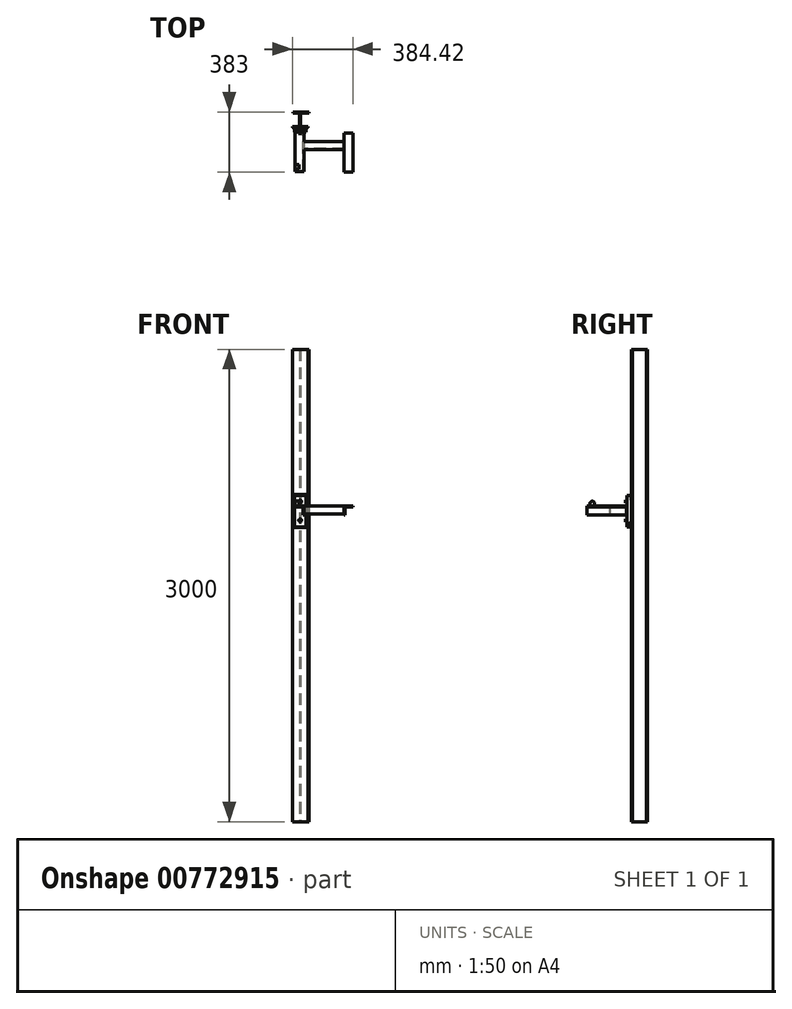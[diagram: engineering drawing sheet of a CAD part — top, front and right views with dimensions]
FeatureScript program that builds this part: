
annotation { "Feature Type Name" : "Feature", "Feature Type Description" : "" }
export const myFeature = defineFeature(function(context is Context, id is Id, definition is map)
    precondition{}
    {
        {
            var Q0;
            Q0=qCreatedBy(makeId("Top.planeOp"),FACE);
            var sketch = newSketch(context, id + "F0", { "sketchPlane" : qUnion([Q0])});
            skLineSegment(sketch, "E0", {"start": v(1.94, 6.65) * mm, "end": v(1.94, 94) * mm});
            skLineSegment(sketch, "E1", {"start": v(1.94, 94) * mm, "end": v(55.47, 94) * mm});
            skLineSegment(sketch, "E2", {"start": v(55.47, 94) * mm, "end": v(55.47, 100) * mm});
            skLineSegment(sketch, "E3", {"start": v(55.47, 100) * mm, "end": v(-44.53, 100) * mm});
            skLineSegment(sketch, "E4", {"start": v(-44.53, 100) * mm, "end": v(-44.53, 94) * mm});
            skLineSegment(sketch, "E5", {"start": v(-44.53, 94) * mm, "end": v(-4.06, 94) * mm});
            skLineSegment(sketch, "E6", {"start": v(-4.06, 94) * mm, "end": v(-4.06, 6.45) * mm});
            skLineSegment(sketch, "E7", {"start": v(-4.06, 6.45) * mm, "end": v(-50, 6.45) * mm});
            skLineSegment(sketch, "E8", {"start": v(-50, 6.45) * mm, "end": v(-50, 0) * mm});
            skLineSegment(sketch, "E9", {"start": v(-50, 0) * mm, "end": v(50, 0) * mm});
            skLineSegment(sketch, "E10", {"start": v(50, 0) * mm, "end": v(50, 6.65) * mm});
            skLineSegment(sketch, "E11", {"start": v(50, 6.65) * mm, "end": v(1.94, 6.65) * mm});
            skSolve(sketch);
        }
        {
            var Q0;
            Q0=makeQuery(id+"F0.imprint","IMPRINT",FACE,{"disambiguationData":[TD([[makeQuery(id+"F0.imprint","IMPRINT",EDGE,{"derivedFrom":sQuery(id+"F0.wireOp",EDGE,"E0")}),1.0]])]});
            extrude(context, id + "F1", {"entities" : qUnion([Q0]), "depth" : 3000 * mm, "offsetDistance" : 25 * mm});
        }
        {
            var Q0;
            Q0=makeQuery(id+"F1.opExtrude","SWEPT_FACE",FACE,{"disambiguationData":[OSD([sQuery(id+"F0.wireOp",EDGE,"E9")])]});
            var sketch = newSketch(context, id + "F2", { "sketchPlane" : qUnion([Q0])});
            skLineSegment(sketch, "E12.bottom", {"start": v(-37.5, 2073.07) * mm, "end": v(37.5, 2073.07) * mm});
            skLineSegment(sketch, "E12.top", {"start": v(-37.5, 1873.07) * mm, "end": v(37.5, 1873.07) * mm});
            skLineSegment(sketch, "E12.left", {"start": v(-37.5, 2073.07) * mm, "end": v(-37.5, 1873.07) * mm});
            skLineSegment(sketch, "E12.right", {"start": v(37.5, 2073.07) * mm, "end": v(37.5, 1873.07) * mm});
            skSolve(sketch);
        }
        {
            var Q0;
            Q0 = qSketchRegion(id + "F2", true);
            extrude(context, id + "F3", {"entities" : qUnion([Q0]), "operationType" : NewBodyOperationType.ADD, "depth" : 20 * mm, "offsetDistance" : 25 * mm});
        }
        {
            var Q0;
            Q0=makeQuery(id+"F3.opExtrude","CAP_FACE",FACE,{"disambiguationData":[OSD([sQuery(id+"F2.wireOp",EDGE,"E12.bottom"),sQuery(id+"F2.wireOp",EDGE,"E12.top"),sQuery(id+"F2.wireOp",EDGE,"E12.left"),sQuery(id+"F2.wireOp",EDGE,"E12.right")])],"isStart":false});
            var sketch = newSketch(context, id + "F4", { "sketchPlane" : qUnion([Q0])});
            skLineSegment(sketch, "E13.bottom", {"start": v(-37.5, 2073.07) * mm, "end": v(37.5, 2073.07) * mm});
            skLineSegment(sketch, "E13.top", {"start": v(-37.5, 1873.07) * mm, "end": v(37.5, 1873.07) * mm});
            skLineSegment(sketch, "E13.left", {"start": v(-37.5, 2073.07) * mm, "end": v(-37.5, 1873.07) * mm});
            skLineSegment(sketch, "E13.right", {"start": v(37.5, 2073.07) * mm, "end": v(37.5, 1873.07) * mm});
            skSolve(sketch);
        }
        {
            var Q0;
            Q0 = qSketchRegion(id + "F4", true);
            extrude(context, id + "F5", {"entities" : qUnion([Q0]), "operationType" : NewBodyOperationType.ADD, "depth" : 9 * mm, "offsetDistance" : 25 * mm});
        }
        {
            var Q0;
            Q0=makeQuery(id+"F5.opExtrude","CAP_FACE",FACE,{"disambiguationData":[OSD([sQuery(id+"F4.wireOp",EDGE,"E13.bottom"),sQuery(id+"F4.wireOp",EDGE,"E13.top"),sQuery(id+"F4.wireOp",EDGE,"E13.left"),sQuery(id+"F4.wireOp",EDGE,"E13.right")])],"isStart":false});
            var sketch = newSketch(context, id + "F6", { "sketchPlane" : qUnion([Q0])});
            skCircle(sketch, "E14", {"center": v(0, 2032.65) * mm, "radius": 9.5 * mm});
            skCircle(sketch, "E15", {"center": v(0, 1914.15) * mm, "radius": 9.29 * mm});
            skPoint(sketch, "E16", {"position": v(0, 2073.07) * mm});
            skSolve(sketch);
        }
        {
            var Q0;
            Q0 = qSketchRegion(id + "F6", true);
            extrude(context, id + "F7", {"entities" : qUnion([Q0]), "operationType" : NewBodyOperationType.ADD, "depth" : 10 * mm, "offsetDistance" : 25 * mm});
        }
        {
            var Q0;
            Q0=makeQuery(id+"F5.opExtrude","CAP_FACE",FACE,{"disambiguationData":[OSD([sQuery(id+"F4.wireOp",EDGE,"E13.bottom"),sQuery(id+"F4.wireOp",EDGE,"E13.top"),sQuery(id+"F4.wireOp",EDGE,"E13.left"),sQuery(id+"F4.wireOp",EDGE,"E13.right")])],"isStart":false});
            var sketch = newSketch(context, id + "F8", { "sketchPlane" : qUnion([Q0])});
            skLineSegment(sketch, "E17.MirrorCS", {"start": v(23.23, 1946.87) * mm, "end": v(16.74, 1946.87) * mm});
            skLineSegment(sketch, "E18.MirrorCS", {"start": v(-31.96, 1998.16) * mm, "end": v(-31.96, 2005.3) * mm});
            skLineSegment(sketch, "E19.MirrorCS", {"start": v(16.74, 1946.87) * mm, "end": v(16.74, 1998.16) * mm});
            skLineSegment(sketch, "E20.MirrorCS", {"start": v(16.74, 1998.16) * mm, "end": v(-31.96, 1998.16) * mm});
            skLineSegment(sketch, "E21.MirrorCS", {"start": v(23.23, 2005.3) * mm, "end": v(23.23, 1946.87) * mm});
            skLineSegment(sketch, "E22.MirrorCS", {"start": v(-31.96, 2005.3) * mm, "end": v(23.23, 2005.3) * mm});
            skSolve(sketch);
        }
        {
            var Q0;
            Q0 = qSketchRegion(id + "F8", true);
            extrude(context, id + "F9", {"entities" : qUnion([Q0]), "operationType" : NewBodyOperationType.ADD, "depth" : 250 * mm, "offsetDistance" : 25 * mm});
        }
        {
            var Q0;
            Q0=makeQuery(id+"F9.opExtrude","SWEPT_FACE",FACE,{"disambiguationData":[OSD([sQuery(id+"F8.wireOp",EDGE,"E21.MirrorCS")])]});
            var sketch = newSketch(context, id + "F10", { "sketchPlane" : qUnion([Q0])});
            skLineSegment(sketch, "E23.MirrorCS", {"start": v(-133, 1955.3) * mm, "end": v(-139, 1955.3) * mm});
            skLineSegment(sketch, "E24.MirrorCS", {"start": v(-89, 1999.3) * mm, "end": v(-89, 2005.3) * mm});
            skLineSegment(sketch, "E25.MirrorCS", {"start": v(-133, 1955.3) * mm, "end": v(-133, 1999.3) * mm});
            skLineSegment(sketch, "E26.MirrorCS", {"start": v(-89, 1999.3) * mm, "end": v(-133, 1999.3) * mm});
            skLineSegment(sketch, "E27.MirrorCS", {"start": v(-139, 2005.3) * mm, "end": v(-139, 1955.3) * mm});
            skLineSegment(sketch, "E28.MirrorCS", {"start": v(-139, 2005.3) * mm, "end": v(-89, 2005.3) * mm});
            skSolve(sketch);
        }
        {
            var Q0;
            Q0 = qSketchRegion(id + "F10", true);
            extrude(context, id + "F11", {"entities" : qUnion([Q0]), "operationType" : NewBodyOperationType.ADD, "depth" : 256 * mm, "offsetDistance" : 25 * mm});
        }
        {
            var Q0;
            Q0=makeQuery(id+"F11.opExtrude","SWEPT_FACE",FACE,{"disambiguationData":[OSD([sQuery(id+"F10.wireOp",EDGE,"E25.MirrorCS")])]});
            var sketch = newSketch(context, id + "F12", { "sketchPlane" : qUnion([Q0])});
            skLineSegment(sketch, "E29.MirrorCS", {"start": v(-279.23, 1946.87) * mm, "end": v(-285.73, 1946.87) * mm});
            skLineSegment(sketch, "E30.MirrorCS", {"start": v(-334.42, 1998.16) * mm, "end": v(-334.42, 2005.3) * mm});
            skLineSegment(sketch, "E31.MirrorCS", {"start": v(-285.73, 1946.87) * mm, "end": v(-285.73, 1998.16) * mm});
            skLineSegment(sketch, "E32.MirrorCS", {"start": v(-285.73, 1998.16) * mm, "end": v(-334.42, 1998.16) * mm});
            skLineSegment(sketch, "E33.MirrorCS", {"start": v(-279.23, 2005.3) * mm, "end": v(-279.23, 1946.87) * mm});
            skLineSegment(sketch, "E34.MirrorCS", {"start": v(-334.42, 2005.3) * mm, "end": v(-279.23, 2005.3) * mm});
            skSolve(sketch);
        }
        {
            var Q0;
            Q0 = qSketchRegion(id + "F12", true);
            extrude(context, id + "F13", {"entities" : qUnion([Q0]), "oppositeDirection" : true, "depth" : 150 * mm, "offsetDistance" : 25 * mm, "hasSecondDirection" : true, "secondDirectionOppositeDirection" : false, "secondDirectionDepth" : 100 * mm});
        }
        {
            var Q0;
            Q0=makeQuery(id+"F1.opExtrude","SWEPT_FACE",FACE,{"disambiguationData":[OSD([sQuery(id+"F0.wireOp",EDGE,"E9")])]});
            var sketch = newSketch(context, id + "F14", { "sketchPlane" : qUnion([Q0])});
            skLineSegment(sketch, "E35.bottom", {"start": v(-43.5, 1904.07) * mm, "end": v(-37.5, 1904.07) * mm});
            skLineSegment(sketch, "E35.top", {"start": v(-43.5, 1873.07) * mm, "end": v(-37.5, 1873.07) * mm});
            skLineSegment(sketch, "E35.left", {"start": v(-43.5, 1904.07) * mm, "end": v(-43.5, 1873.07) * mm});
            skLineSegment(sketch, "E35.right", {"start": v(-37.5, 1904.07) * mm, "end": v(-37.5, 1873.07) * mm});
            skLineSegment(sketch, "E36.bottom", {"start": v(-43.5, 1873.07) * mm, "end": v(43.5, 1873.07) * mm});
            skLineSegment(sketch, "E36.top", {"start": v(-43.5, 1867.07) * mm, "end": v(43.5, 1867.07) * mm});
            skLineSegment(sketch, "E36.left", {"start": v(-43.5, 1873.07) * mm, "end": v(-43.5, 1867.07) * mm});
            skLineSegment(sketch, "E36.right", {"start": v(43.5, 1873.07) * mm, "end": v(43.5, 1867.07) * mm});
            skLineSegment(sketch, "E37.bottom", {"start": v(37.5, 1904.07) * mm, "end": v(43.5, 1904.07) * mm});
            skLineSegment(sketch, "E37.top", {"start": v(37.5, 1873.07) * mm, "end": v(43.5, 1873.07) * mm});
            skLineSegment(sketch, "E37.left", {"start": v(37.5, 1904.07) * mm, "end": v(37.5, 1873.07) * mm});
            skLineSegment(sketch, "E37.right", {"start": v(43.5, 1904.07) * mm, "end": v(43.5, 1873.07) * mm});
            skLineSegment(sketch, "E38.bottom", {"start": v(-37.5, 2042.07) * mm, "end": v(-43.5, 2042.07) * mm});
            skLineSegment(sketch, "E38.top", {"start": v(-37.5, 2073.07) * mm, "end": v(-43.5, 2073.07) * mm});
            skLineSegment(sketch, "E38.left", {"start": v(-37.5, 2042.07) * mm, "end": v(-37.5, 2073.07) * mm});
            skLineSegment(sketch, "E38.right", {"start": v(-43.5, 2042.07) * mm, "end": v(-43.5, 2073.07) * mm});
            skLineSegment(sketch, "E39.bottom", {"start": v(-43.5, 2073.07) * mm, "end": v(43.5, 2073.07) * mm});
            skLineSegment(sketch, "E39.top", {"start": v(-43.5, 2079.07) * mm, "end": v(43.5, 2079.07) * mm});
            skLineSegment(sketch, "E39.left", {"start": v(-43.5, 2073.07) * mm, "end": v(-43.5, 2079.07) * mm});
            skLineSegment(sketch, "E39.right", {"start": v(43.5, 2073.07) * mm, "end": v(43.5, 2079.07) * mm});
            skLineSegment(sketch, "E40.bottom", {"start": v(43.5, 2073.07) * mm, "end": v(37.5, 2073.07) * mm});
            skLineSegment(sketch, "E40.top", {"start": v(43.5, 2042.07) * mm, "end": v(37.5, 2042.07) * mm});
            skLineSegment(sketch, "E40.left", {"start": v(43.5, 2073.07) * mm, "end": v(43.5, 2042.07) * mm});
            skLineSegment(sketch, "E40.right", {"start": v(37.5, 2073.07) * mm, "end": v(37.5, 2042.07) * mm});
            skSolve(sketch);
        }
        {
            var Q0;
            Q0=makeQuery(id+"F14.imprint","IMPRINT",FACE,{"disambiguationData":[TD([[makeQuery(id+"F14.imprint","IMPRINT",EDGE,{"derivedFrom":sQuery(id+"F14.wireOp",EDGE,"E38.bottom")}),-1.0]])]});
            var Q1;
            Q1=makeQuery(id+"F14.imprint","IMPRINT",FACE,{"disambiguationData":[TD([[makeQuery(id+"F14.imprint","IMPRINT",EDGE,{"derivedFrom":sQuery(id+"F14.wireOp",EDGE,"E39.top")}),-1.0]])]});
            var Q2;
            Q2=makeQuery(id+"F14.imprint","IMPRINT",FACE,{"disambiguationData":[TD([[makeQuery(id+"F14.imprint","IMPRINT",EDGE,{"derivedFrom":sQuery(id+"F14.wireOp",EDGE,"E40.bottom")}),1.0]])]});
            var Q3;
            Q3=makeQuery(id+"F14.imprint","IMPRINT",FACE,{"disambiguationData":[TD([[makeQuery(id+"F14.imprint","IMPRINT",EDGE,{"derivedFrom":sQuery(id+"F14.wireOp",EDGE,"E37.bottom")}),-1.0]])]});
            var Q4;
            Q4=makeQuery(id+"F14.imprint","IMPRINT",FACE,{"disambiguationData":[TD([[makeQuery(id+"F14.imprint","IMPRINT",EDGE,{"derivedFrom":sQuery(id+"F14.wireOp",EDGE,"E36.top")}),1.0]])]});
            var Q5;
            Q5=makeQuery(id+"F14.imprint","IMPRINT",FACE,{"disambiguationData":[TD([[makeQuery(id+"F14.imprint","IMPRINT",EDGE,{"derivedFrom":sQuery(id+"F14.wireOp",EDGE,"E35.bottom")}),-1.0]])]});
            extrude(context, id + "F15", {"entities" : qUnion([Q0, Q1, Q2, Q3, Q4, Q5]), "operationType" : NewBodyOperationType.ADD, "depth" : 6 * mm, "offsetDistance" : 25 * mm});
        }
        {
            var Q0;
            Q0=makeQuery(id+"F15.opExtrude","CAP_EDGE",EDGE,{"disambiguationData":[OSD([sQuery(id+"F14.wireOp",EDGE,"E38.right"),sQuery(id+"F14.wireOp",EDGE,"E39.left")])],"isStart":false});
            var Q1;
            Q1=makeQuery(id+"F15.opExtrude","CAP_EDGE",EDGE,{"disambiguationData":[OSD([sQuery(id+"F14.wireOp",EDGE,"E39.top")])],"isStart":false});
            var Q2;
            Q2=makeQuery(id+"F15.opExtrude","CAP_EDGE",EDGE,{"disambiguationData":[OSD([sQuery(id+"F14.wireOp",EDGE,"E39.right"),sQuery(id+"F14.wireOp",EDGE,"E40.left")])],"isStart":false});
            var Q3;
            Q3=makeQuery(id+"F15.opExtrude","CAP_EDGE",EDGE,{"disambiguationData":[OSD([sQuery(id+"F14.wireOp",EDGE,"E36.right"),sQuery(id+"F14.wireOp",EDGE,"E37.right")])],"isStart":false});
            var Q4;
            Q4=makeQuery(id+"F15.opExtrude","CAP_EDGE",EDGE,{"disambiguationData":[OSD([sQuery(id+"F14.wireOp",EDGE,"E36.top")])],"isStart":false});
            var Q5;
            Q5=makeQuery(id+"F15.opExtrude","CAP_EDGE",EDGE,{"disambiguationData":[OSD([sQuery(id+"F14.wireOp",EDGE,"E35.left"),sQuery(id+"F14.wireOp",EDGE,"E36.left")])],"isStart":false});
            fillet(context, id + "F16", {"entities" : qUnion([Q0, Q1, Q2, Q3, Q4, Q5]), "radius" : 5 * mm, "tangentPropagation" : true, "allowEdgeOverflow" : false});
        }
        {
            var Q0;
            Q0=makeQuery(id+"F9.opExtrude","SWEPT_FACE",FACE,{"disambiguationData":[OSD([sQuery(id+"F8.wireOp",EDGE,"E18.MirrorCS")])]});
            var sketch = newSketch(context, id + "F17", { "sketchPlane" : qUnion([Q0])});
            skLineSegment(sketch, "E41", {"start": v(29, 2005.3) * mm, "end": v(279, 2005.3) * mm});
            skLineSegment(sketch, "E42", {"start": v(279, 2005.3) * mm, "end": v(249, 2005.3) * mm});
            skCircle(sketch, "E43", {"center": v(249, 2020.3) * mm, "radius": 15 * mm});
            skSolve(sketch);
        }
        {
            var Q0;
            Q0=makeQuery(id+"F17.imprint","IMPRINT",FACE,{"disambiguationData":[TD([[makeQuery(id+"F17.imprint","IMPRINT",EDGE,{"derivedFrom":sQuery(id+"F17.wireOp",EDGE,"E43")}),1.0]])]});
            extrude(context, id + "F18", {"entities" : qUnion([Q0]), "oppositeDirection" : true, "depth" : 25 * mm, "offsetDistance" : 25 * mm});
        }
    });
